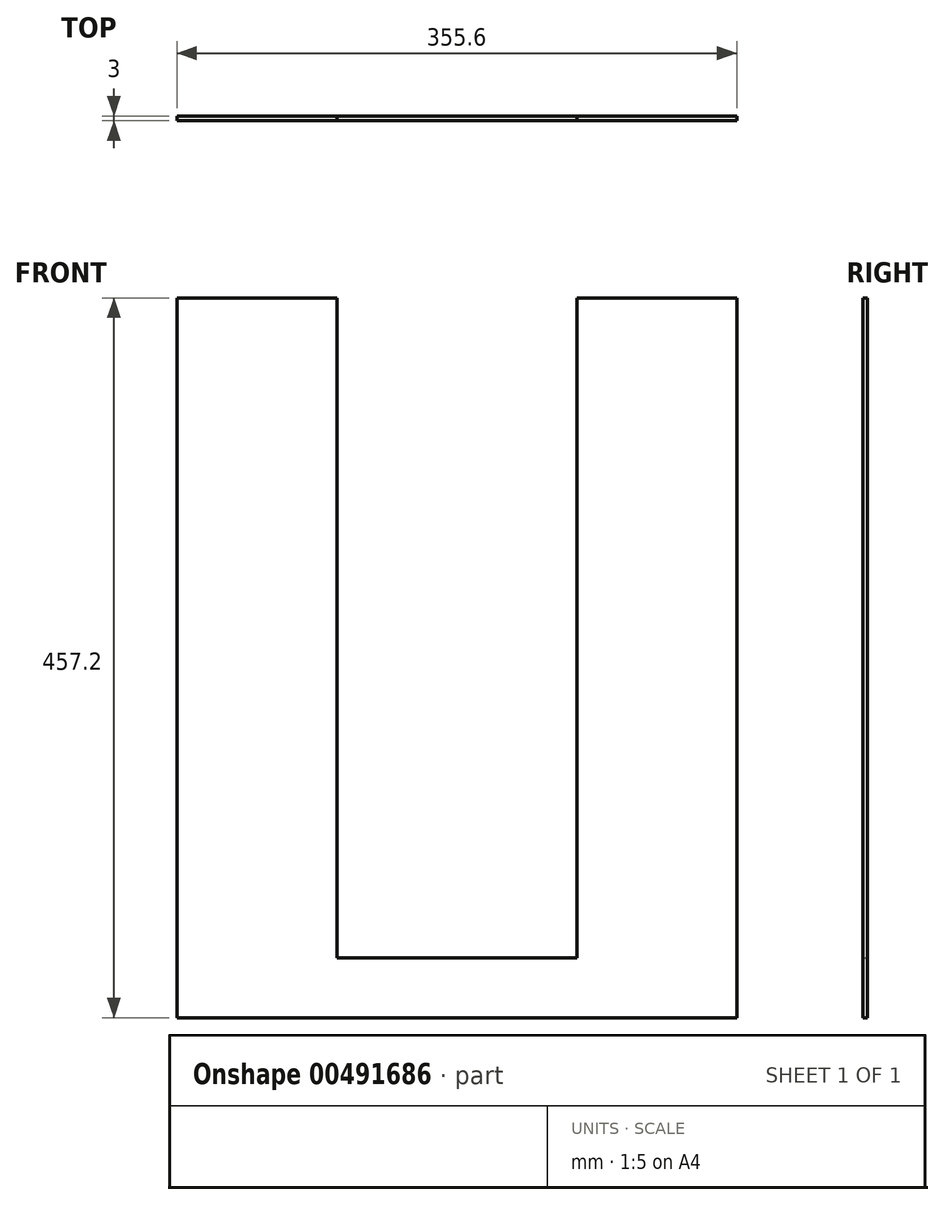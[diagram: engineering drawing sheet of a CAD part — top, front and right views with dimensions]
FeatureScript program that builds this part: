
annotation { "Feature Type Name" : "Feature", "Feature Type Description" : "" }
export const myFeature = defineFeature(function(context is Context, id is Id, definition is map)
    precondition{}
    {
        {
            var Q0;
            Q0=qCreatedBy(makeId("Front.planeOp"),FACE);
            var sketch = newSketch(context, id + "F0", { "sketchPlane" : qUnion([Q0])});
            skLineSegment(sketch, "E0.bottom", {"start": v(-177.8, 251.48) * mm, "end": v(177.8, 251.48) * mm});
            skLineSegment(sketch, "E0.top", {"start": v(-177.8, -205.72) * mm, "end": v(177.8, -205.72) * mm});
            skLineSegment(sketch, "E0.left", {"start": v(-177.8, 251.48) * mm, "end": v(-177.8, -205.72) * mm});
            skLineSegment(sketch, "E0.right", {"start": v(177.8, 251.48) * mm, "end": v(177.8, -205.72) * mm});
            skLineSegment(sketch, "E1", {"start": v(-177.8, 251.48) * mm, "end": v(0, 251.48) * mm});
            skLineSegment(sketch, "E2", {"start": v(0, 251.48) * mm, "end": v(177.8, 251.48) * mm});
            skLineSegment(sketch, "E3", {"start": v(0, 251.48) * mm, "end": v(-76.2, 251.48) * mm});
            skLineSegment(sketch, "E4", {"start": v(0, 251.48) * mm, "end": v(76.2, 251.48) * mm});
            skLineSegment(sketch, "E5", {"start": v(-76.2, 251.48) * mm, "end": v(-76.2, -167.62) * mm});
            skLineSegment(sketch, "E6", {"start": v(-76.2, -167.62) * mm, "end": v(76.2, -167.62) * mm});
            skLineSegment(sketch, "E7", {"start": v(76.2, -167.62) * mm, "end": v(76.2, 251.48) * mm});
            skSolve(sketch);
        }
        {
            var Q0;
            Q0=makeQuery(id+"F0.imprint","IMPRINT",FACE,{"disambiguationData":[TD([[makeQuery(id+"F0.imprint","IMPRINT",EDGE,{"derivedFrom":sQuery(id+"F0.wireOp",EDGE,"E0.top")}),1.0]])]});
            extrude(context, id + "F1", {"entities" : qUnion([Q0]), "depth" : 3 * mm});
        }
    });
